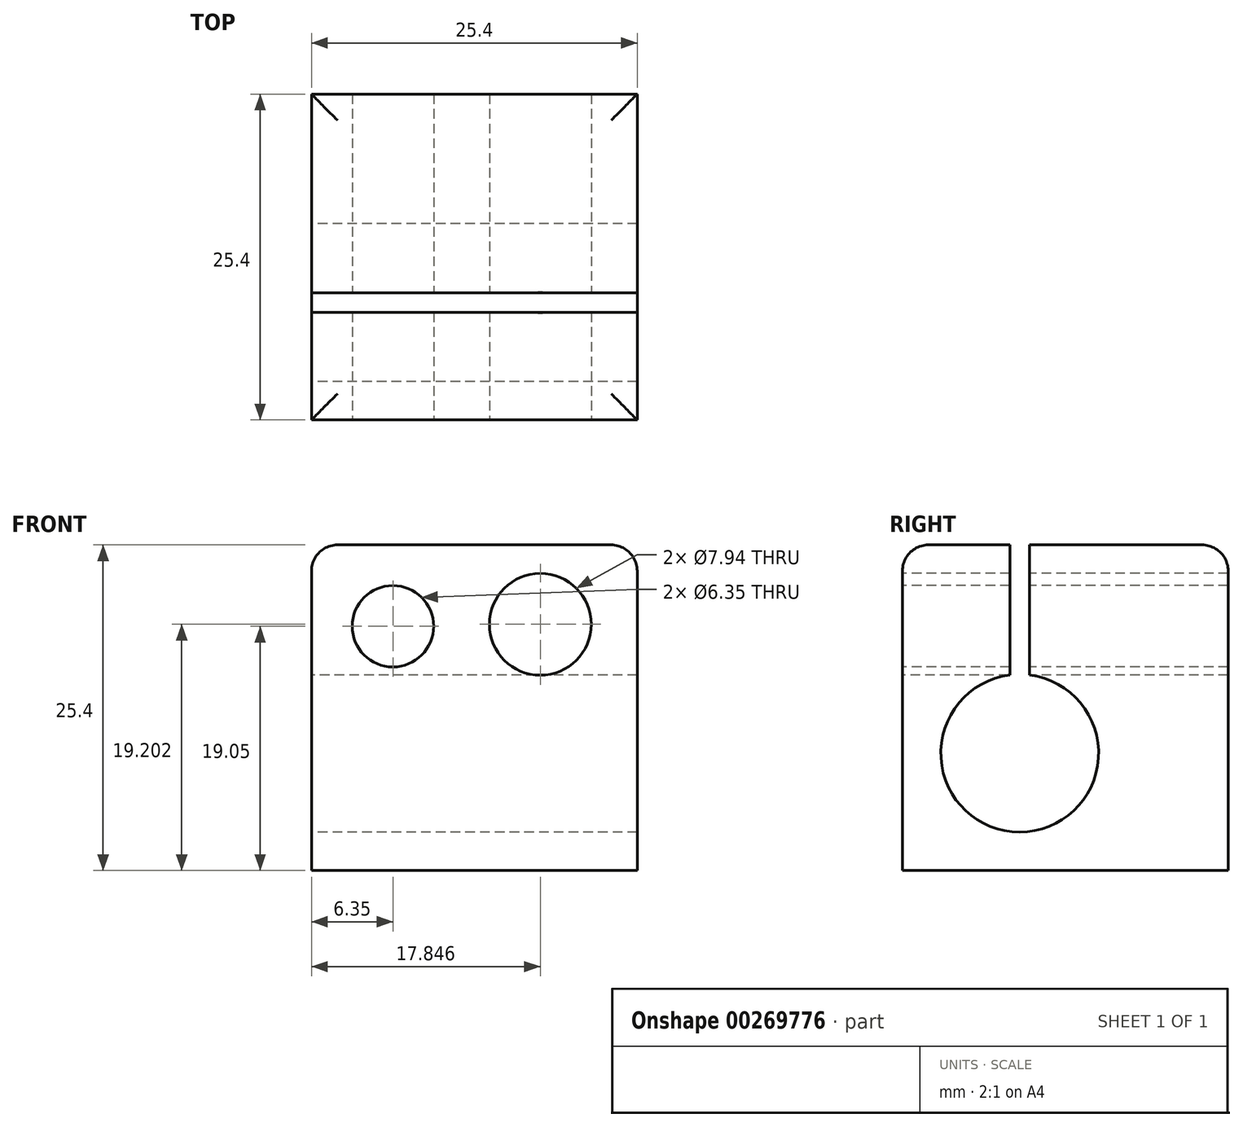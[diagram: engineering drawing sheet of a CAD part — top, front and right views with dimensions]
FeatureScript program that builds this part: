
annotation { "Feature Type Name" : "Feature", "Feature Type Description" : "" }
export const myFeature = defineFeature(function(context is Context, id is Id, definition is map)
    precondition{}
    {
        {
            var Q0;
            Q0=qCreatedBy(makeId("Right.planeOp"),FACE);
            var sketch = newSketch(context, id + "F0", { "sketchPlane" : qUnion([Q0])});
            skLineSegment(sketch, "E0.bottom", {"start": v(12.7, 12.7) * mm, "end": v(-2.8, 12.7) * mm});
            skLineSegment(sketch, "E0.top", {"start": v(12.7, -12.7) * mm, "end": v(-12.7, -12.7) * mm});
            skLineSegment(sketch, "E0.left", {"start": v(12.7, 12.7) * mm, "end": v(12.7, -12.7) * mm});
            skLineSegment(sketch, "E0.right", {"start": v(-12.7, 12.7) * mm, "end": v(-12.7, -12.7) * mm});
            skPoint(sketch, "E0.middle", {"position": v(0, 0) * mm});
            skArc(sketch, "E1", {"start": v(-4.32, 2.55) * mm, "mid": v(-3.56, -9.7) * mm, "end": v(-2.8, 2.55) * mm});
            skLineSegment(sketch, "E2.0", {"start": v(-2.8, 2.55) * mm, "end": v(-2.8, 12.7) * mm});
            skLineSegment(sketch, "E3.0", {"start": v(-4.32, 2.55) * mm, "end": v(-4.32, 12.7) * mm});
            skLineSegment(sketch, "E4.trimOffspring", {"start": v(-4.32, 12.7) * mm, "end": v(-12.7, 12.7) * mm});
            skSolve(sketch);
        }
        {
            var Q0;
            Q0=makeQuery(id+"F0.imprint","IMPRINT",FACE,{"disambiguationData":[TD([[makeQuery(id+"F0.imprint","IMPRINT",EDGE,{"derivedFrom":sQuery(id+"F0.wireOp",EDGE,"E0.bottom")}),1.0]])]});
            extrude(context, id + "F1", {"entities" : qUnion([Q0]), "depth" : 25.4 * mm});
        }
        {
            var Q0;
            Q0=makeQuery(id+"F1.opExtrude","SWEPT_FACE",FACE,{"disambiguationData":[OSD([sQuery(id+"F0.wireOp",EDGE,"E0.right")])]});
            var sketch = newSketch(context, id + "F2", { "sketchPlane" : qUnion([Q0])});
            skCircle(sketch, "E5", {"center": v(6.35, 6.35) * mm, "radius": 3.18 * mm});
            skCircle(sketch, "E6", {"center": v(17.85, 6.5) * mm, "radius": 3.97 * mm});
            skSolve(sketch);
        }
        {
            var Q0;
            Q0 = qSketchRegion(id + "F2", true);
            extrude(context, id + "F3", {"entities" : qUnion([Q0]), "operationType" : NewBodyOperationType.REMOVE, "endBound" : BoundingType.THROUGH_ALL, "oppositeDirection" : true, "depth" : 25.4 * mm});
        }
        {
            var Q0;
            Q0=makeQuery(id+"F1.opExtrude","CAP_EDGE",EDGE,{"disambiguationData":[OSD([sQuery(id+"F0.wireOp",EDGE,"E0.bottom")])],"isStart":true});
            var Q1;
            Q1=makeQuery(id+"F1.opExtrude","SWEPT_EDGE",EDGE,{"disambiguationData":[OSD([sQuery(id+"F0.wireOp",EDGE,"E0.bottom"),sQuery(id+"F0.wireOp",EDGE,"E0.left")])]});
            var Q2;
            Q2=makeQuery(id+"F1.opExtrude","CAP_EDGE",EDGE,{"disambiguationData":[OSD([sQuery(id+"F0.wireOp",EDGE,"E0.bottom")])],"isStart":false});
            var Q3;
            Q3=makeQuery(id+"F1.opExtrude","CAP_EDGE",EDGE,{"disambiguationData":[OSD([sQuery(id+"F0.wireOp",EDGE,"E4.trimOffspring")])],"isStart":false});
            var Q4;
            Q4=makeQuery(id+"F1.opExtrude","SWEPT_EDGE",EDGE,{"disambiguationData":[OSD([sQuery(id+"F0.wireOp",EDGE,"E0.right"),sQuery(id+"F0.wireOp",EDGE,"E4.trimOffspring")])]});
            var Q5;
            Q5=makeQuery(id+"F1.opExtrude","CAP_EDGE",EDGE,{"disambiguationData":[OSD([sQuery(id+"F0.wireOp",EDGE,"E4.trimOffspring")])],"isStart":true});
            fillet(context, id + "F4", {"entities" : qUnion([Q0, Q1, Q2, Q3, Q4, Q5]), "radius" : 2.03 * mm, "tangentPropagation" : true, "allowEdgeOverflow" : false});
        }
    });
